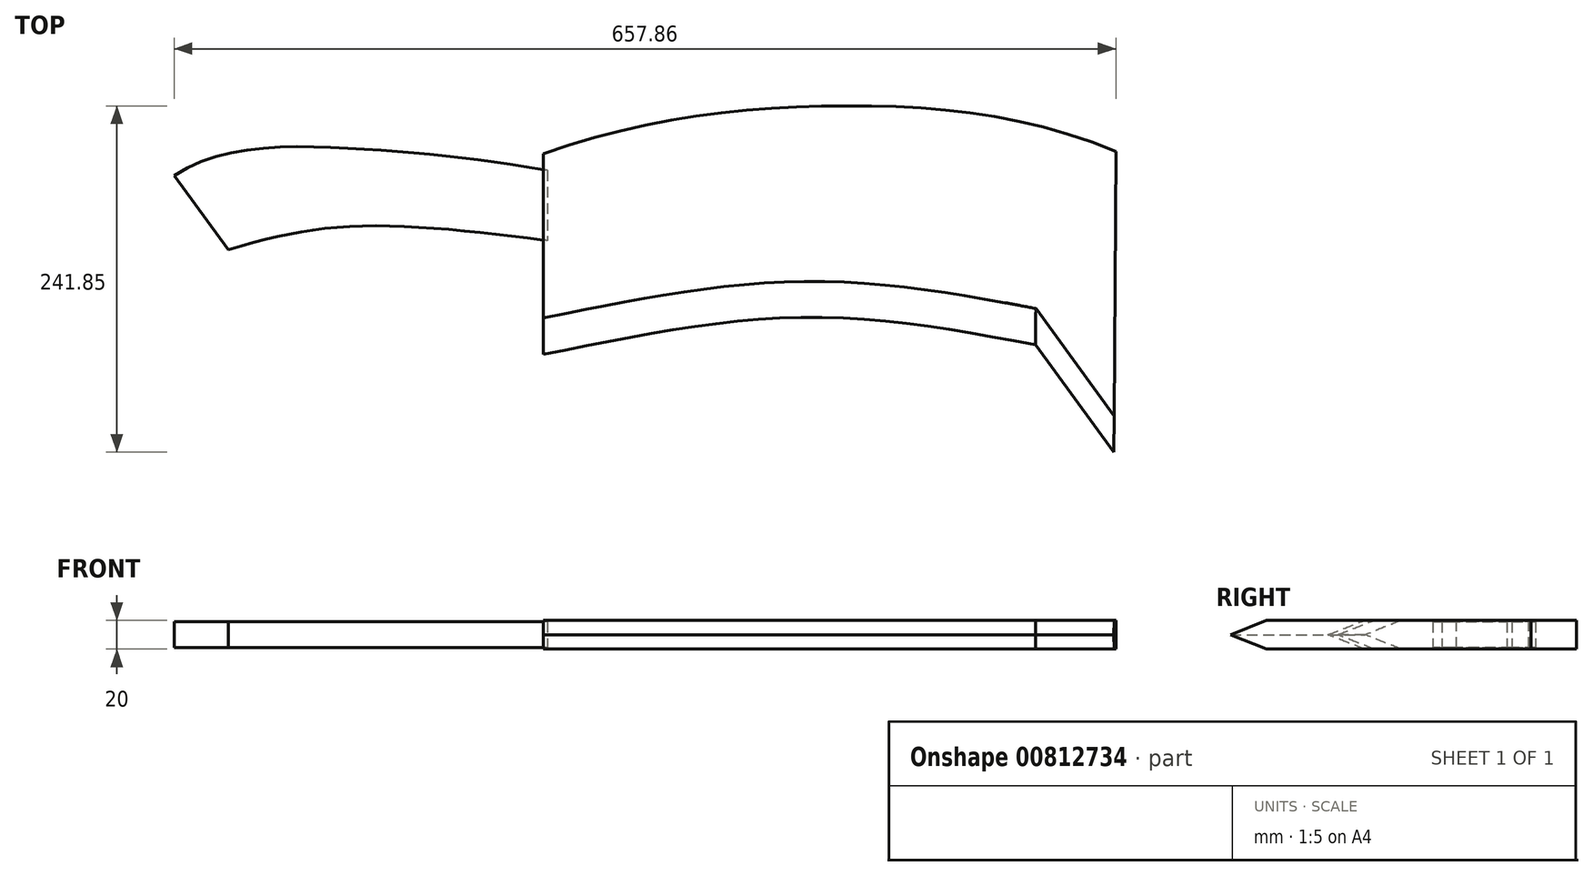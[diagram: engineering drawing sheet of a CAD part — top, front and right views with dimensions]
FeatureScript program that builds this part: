
annotation { "Feature Type Name" : "Feature", "Feature Type Description" : "" }
export const myFeature = defineFeature(function(context is Context, id is Id, definition is map)
    precondition{}
    {
        {
            var Q0;
            Q0=qCreatedBy(makeId("Top.planeOp"),FACE);
            var sketch = newSketch(context, id + "F0", { "sketchPlane" : qUnion([Q0])});
            skFitSpline(sketch, "E0", {"points": [v(-190.82, 30.41) * mm, v(15.49, 63.98) * mm, v(209.18, 32.17) * mm], "startDerivative": vector(414.46, 148.7) * mm, "endDerivative": vector(385.36, -161) * mm});
            skFitSpline(sketch, "E1", {"points": [v(-190.82, -109.59) * mm, v(-7.52, -83.63) * mm, v(153.22, -102.91) * mm], "startDerivative": vector(360.5, 73.54) * mm, "endDerivative": vector(327.83, -61.68) * mm});
            skLineSegment(sketch, "E2", {"start": v(153.22, -102.91) * mm, "end": v(207.7, -177.83) * mm});
            skLineSegment(sketch, "E3", {"start": v(-190.82, 30.41) * mm, "end": v(-190.82, -109.59) * mm});
            skLineSegment(sketch, "E4", {"start": v(209.18, 32.17) * mm, "end": v(207.7, -177.83) * mm});
            skSolve(sketch);
        }
        {
            var Q0;
            Q0=makeQuery(id+"F0.imprint","IMPRINT",FACE,{"disambiguationData":[TD([[makeQuery(id+"F0.imprint","IMPRINT",EDGE,{"derivedFrom":sQuery(id+"F0.wireOp",EDGE,"E0")}),-1.0]])]});
            extrude(context, id + "F1", {"entities" : qUnion([Q0]), "endBound" : BoundingType.SYMMETRIC, "depth" : 20 * mm, "offsetDistance" : 25 * mm});
        }
        {
            var Q0;
            Q0=makeQuery(id+"F1.opExtrude","CAP_EDGE",EDGE,{"disambiguationData":[OSD([sQuery(id+"F0.wireOp",EDGE,"E1")])],"isStart":false});
            var Q1;
            Q1=makeQuery(id+"F1.opExtrude","CAP_EDGE",EDGE,{"disambiguationData":[OSD([sQuery(id+"F0.wireOp",EDGE,"E1")])],"isStart":true});
            chamfer(context, id + "F2", {"entities" : qUnion([Q0, Q1]), "chamferType" : ChamferType.TWO_OFFSETS, "width1" : 25 * mm, "oppositeDirection" : false, "width2" : 10 * mm, "tangentPropagation" : true});
        }
        {
            var Q0;
            Q0=makeQuery(id+"F1.opExtrude","CAP_EDGE",EDGE,{"disambiguationData":[OSD([sQuery(id+"F0.wireOp",EDGE,"E2")])],"isStart":false});
            var Q1;
            Q1=makeQuery(id+"F1.opExtrude","CAP_EDGE",EDGE,{"disambiguationData":[OSD([sQuery(id+"F0.wireOp",EDGE,"E2")])],"isStart":true});
            chamfer(context, id + "F3", {"entities" : qUnion([Q0, Q1]), "chamferType" : ChamferType.TWO_OFFSETS, "width1" : 15 * mm, "oppositeDirection" : false, "width2" : 10 * mm, "tangentPropagation" : true});
        }
        {
            var Q0;
            Q0=qCreatedBy(makeId("Top.planeOp"),FACE);
            var sketch = newSketch(context, id + "F4", { "sketchPlane" : qUnion([Q0])});
            skFitSpline(sketch, "E5", {"points": [v(-190.82, 18.99) * mm, v(-324.6, 34.08) * mm, v(-451.68, 15.2) * mm], "startDerivative": vector(-270.64, 46.88) * mm, "endDerivative": vector(-206.24, -137.5) * mm});
            skFitSpline(sketch, "E6", {"points": [v(-190.82, -30.09) * mm, v(-324.6, -20.02) * mm, v(-413.93, -36.38) * mm], "startDerivative": vector(-257.9, 33.32) * mm, "endDerivative": vector(-211.93, -61.76) * mm});
            skLineSegment(sketch, "E7", {"start": v(-413.93, -36.38) * mm, "end": v(-451.68, 15.2) * mm});
            skLineSegment(sketch, "E8", {"start": v(-190.82, 18.99) * mm, "end": v(-190.82, -30.09) * mm});
            skSolve(sketch);
        }
        {
            var Q0;
            Q0 = qSketchRegion(id + "F4", true);
            extrude(context, id + "F5", {"entities" : qUnion([Q0]), "endBound" : BoundingType.SYMMETRIC, "depth" : 18 * mm, "offsetDistance" : 25 * mm});
        }
        {
            var Q0;
            Q0=makeQuery(id+"F5.opExtrude","SWEPT_BODY",BODY,{"disambiguationData":[OSD([sQuery(id+"F4.wireOp",EDGE,"E5"),sQuery(id+"F4.wireOp",EDGE,"E6"),sQuery(id+"F4.wireOp",EDGE,"E7"),sQuery(id+"F4.wireOp",EDGE,"E8")])]});
            transform(context, id + "F6", {"entities" : qUnion([Q0]), "transformType" : TransformType.TRANSLATION_3D, "dx" : 3 * mm, "dy" : 0 * mm, "dz" : 0 * mm, "makeCopy" : false});
        }
    });
